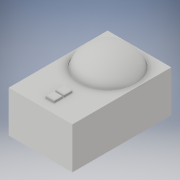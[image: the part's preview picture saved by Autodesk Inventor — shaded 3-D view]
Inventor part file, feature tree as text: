
AUTODESK INVENTOR PART (.ipt)
format: ipt  version: 2017 (Build 210142000, 142)  size: 242,688 bytes
history: native  units: in
note: dims shown in document units (in); Inventor stores cm internally (conversion verified against a paired STEP export)
features: other x6, sketch x5, extrude x4
ambient origin geometry x8: Origin, YZ Plane, XZ Plane, XY Plane, X Axis, Y Axis, Z Axis, Center Point
bodies: Body1 (feature_tree), Body2 (feature_tree), Body3 (feature_tree)
feature tree (15):
  other  "cube for ball"
  sketch  "Sketch1"  dims[d0=3.069in d1=0.136in]
  extrude  "cube to cut from"  Depth=0.136in
  other  "cut out for mouse ball"
  other  "mouse ball"
  extrude  "extention"  Depth=1.8065in
  extrude  "button hole"  Depth=3.613in
  other  "button in hole"
  extrude  "button"  Depth=0.136in
  sketch  "Sketch2"  dims[d3=1.8065in d4=1.8065in]
  other  "ball"
  sketch  "Sketch3"  dims[d5=1.1239in d8=3.613in]
  sketch  "Sketch4"  dims[d9=0.0in d10=0.136in]
  sketch  "Sketch5"  dims[d11=0.02in d17=3.381in d18=180.0deg d19=3.613in d20=180.0deg d21=2.0in d22=0.0in d23=0.52in d24=0.52in d25=1.116in d27=0.1in d28=0.0in d30=0.02in d31=0.02in d32=0.02in d33=0.02in d36=-0.05in d37=0.15in d38=0.0in d39=2.116in d40=0.52in d41=0.52in d42=0.529in d43=0.02in d44=0.02in d45=0.02in d46=0.02in d47=0.033in]
  other  "solid button"
